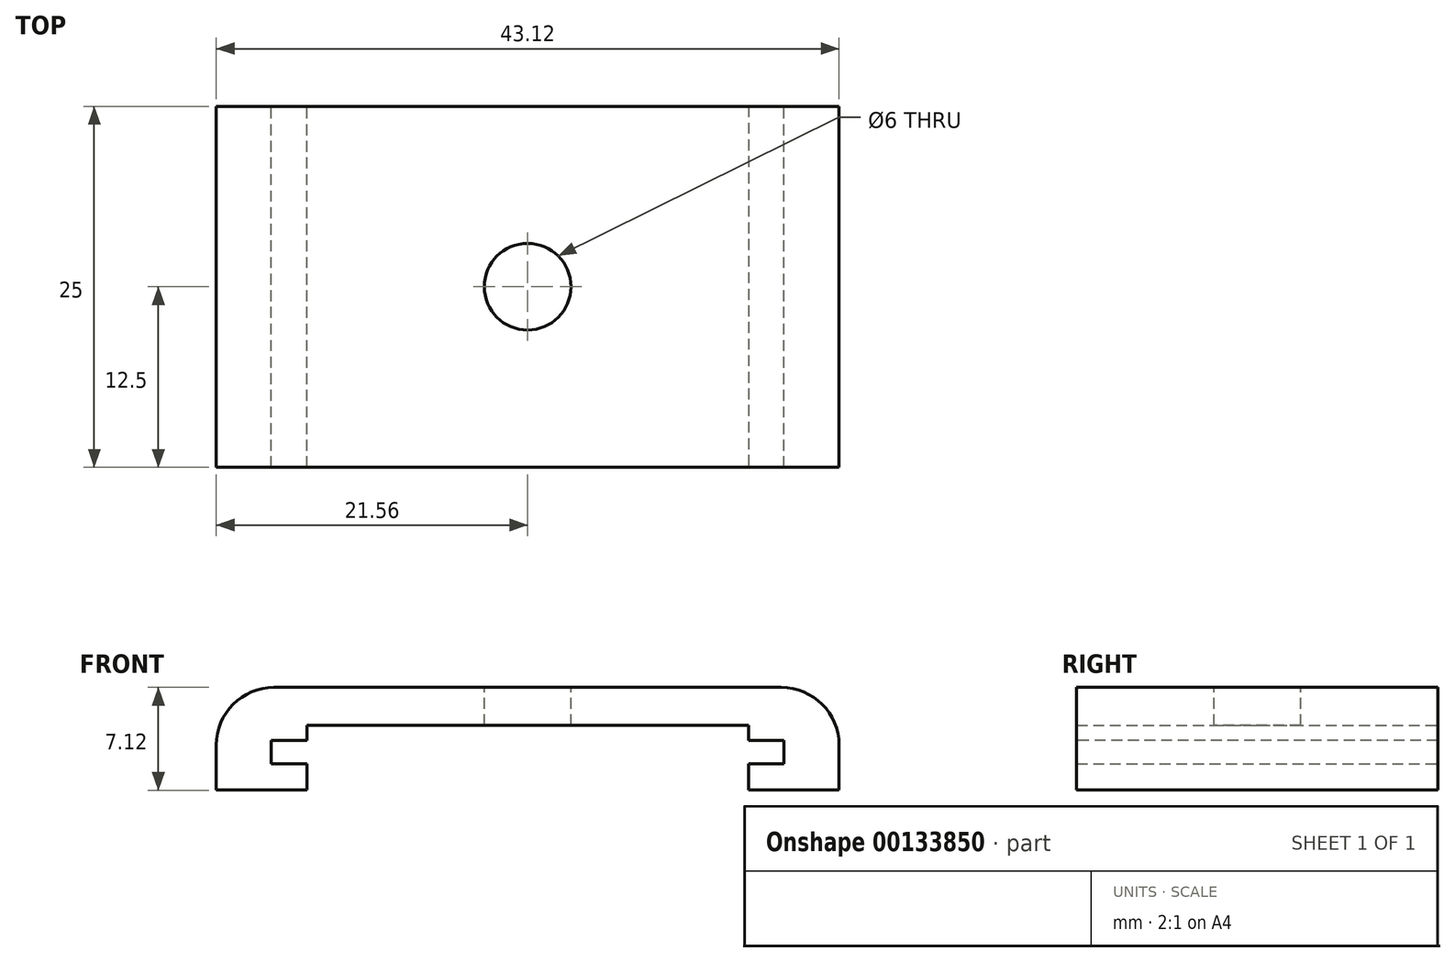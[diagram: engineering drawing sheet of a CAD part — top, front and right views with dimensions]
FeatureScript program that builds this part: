
annotation { "Feature Type Name" : "Feature", "Feature Type Description" : "" }
export const myFeature = defineFeature(function(context is Context, id is Id, definition is map)
    precondition{}
    {
        {
            var Q0;
            Q0=qCreatedBy(makeId("Front.planeOp"),FACE);
            var sketch = newSketch(context, id + "F0", { "sketchPlane" : qUnion([Q0])});
            skLineSegment(sketch, "E0", {"start": v(-17.75, 13.3) * mm, "end": v(-14.55, 13.3) * mm});
            skLineSegment(sketch, "E1", {"start": v(-13.65, 12.4) * mm, "end": v(-13.65, 0.9) * mm});
            skLineSegment(sketch, "E2", {"start": v(-12.75, 0) * mm, "end": v(0, 0) * mm});
            skLineSegment(sketch, "E3.0", {"start": v(-11.15, 1.6) * mm, "end": v(0, 1.6) * mm});
            skLineSegment(sketch, "E3.1", {"start": v(-12.05, 13.7) * mm, "end": v(-12.05, 2.5) * mm});
            skLineSegment(sketch, "E3.2", {"start": v(-17.75, 14.9) * mm, "end": v(-13.25, 14.9) * mm});
            skLineSegment(sketch, "E4", {"start": v(-17.75, 13.3) * mm, "end": v(-17.75, 14.9) * mm});
            skLineSegment(sketch, "E5.MirrorCS", {"start": v(11.15, 1.6) * mm, "end": v(0, 1.6) * mm});
            skLineSegment(sketch, "E6.MirrorCS", {"start": v(12.75, 0) * mm, "end": v(0, 0) * mm});
            skLineSegment(sketch, "E7.MirrorCS", {"start": v(12.05, 13.7) * mm, "end": v(12.05, 2.5) * mm});
            skLineSegment(sketch, "E8.MirrorCS", {"start": v(13.65, 12.4) * mm, "end": v(13.65, 0.9) * mm});
            skLineSegment(sketch, "E9.MirrorCS", {"start": v(17.75, 13.3) * mm, "end": v(14.55, 13.3) * mm});
            skLineSegment(sketch, "E10.MirrorCS", {"start": v(17.75, 14.9) * mm, "end": v(13.25, 14.9) * mm});
            skLineSegment(sketch, "E11.MirrorCS", {"start": v(17.75, 13.3) * mm, "end": v(17.75, 14.9) * mm});
            skPoint(sketch, "E12.visualSharp", {"position": v(-13.65, 13.3) * mm});
            skArc(sketch, "E12.filletArc", {"start": v(-13.65, 12.4) * mm, "mid": v(-13.91, 13.04) * mm, "end": v(-14.55, 13.3) * mm});
            skPoint(sketch, "E13.visualSharp", {"position": v(-12.05, 14.9) * mm});
            skArc(sketch, "E13.filletArc", {"start": v(-12.05, 13.7) * mm, "mid": v(-12.4, 14.55) * mm, "end": v(-13.25, 14.9) * mm});
            skPoint(sketch, "E14.visualSharp", {"position": v(-13.65, 0) * mm});
            skArc(sketch, "E14.filletArc", {"start": v(-13.65, 0.9) * mm, "mid": v(-13.39, 0.26) * mm, "end": v(-12.75, 0) * mm});
            skPoint(sketch, "E15.visualSharp", {"position": v(-12.05, 1.6) * mm});
            skArc(sketch, "E15.filletArc", {"start": v(-12.05, 2.5) * mm, "mid": v(-11.79, 1.86) * mm, "end": v(-11.15, 1.6) * mm});
            skPoint(sketch, "E16.visualSharp", {"position": v(13.65, 0) * mm});
            skArc(sketch, "E16.filletArc", {"start": v(12.75, 0) * mm, "mid": v(13.39, 0.26) * mm, "end": v(13.65, 0.9) * mm});
            skPoint(sketch, "E17.visualSharp", {"position": v(12.05, 1.6) * mm});
            skArc(sketch, "E17.filletArc", {"start": v(11.15, 1.6) * mm, "mid": v(11.79, 1.86) * mm, "end": v(12.05, 2.5) * mm});
            skPoint(sketch, "E18.visualSharp", {"position": v(12.05, 14.9) * mm});
            skArc(sketch, "E18.filletArc", {"start": v(13.25, 14.9) * mm, "mid": v(12.4, 14.55) * mm, "end": v(12.05, 13.7) * mm});
            skPoint(sketch, "E19.visualSharp", {"position": v(13.65, 13.3) * mm});
            skArc(sketch, "E19.filletArc", {"start": v(14.55, 13.3) * mm, "mid": v(13.91, 13.04) * mm, "end": v(13.65, 12.4) * mm});
            skSolve(sketch);
        }
        {
            var Q0;
            Q0 = qSketchRegion(id + "F0", true);
            extrude(context, id + "F1", {"entities" : qUnion([Q0]), "depth" : 50 * mm});
        }
        {
            var Q0;
            Q0=qCreatedBy(makeId("Front.planeOp"),FACE);
            var sketch = newSketch(context, id + "F2", { "sketchPlane" : qUnion([Q0])});
            skLineSegment(sketch, "E20", {"start": v(-15.28, 11.46) * mm, "end": v(-21.56, 11.46) * mm});
            skLineSegment(sketch, "E21", {"start": v(-21.56, 11.46) * mm, "end": v(-21.56, 14.58) * mm});
            skLineSegment(sketch, "E22", {"start": v(-17.56, 18.58) * mm, "end": v(0, 18.58) * mm});
            skLineSegment(sketch, "E23", {"start": v(-15.28, 11.46) * mm, "end": v(-15.28, 15.95) * mm});
            skLineSegment(sketch, "E24", {"start": v(-15.28, 15.95) * mm, "end": v(0, 15.95) * mm});
            skPoint(sketch, "E25.visualSharp", {"position": v(-21.56, 18.58) * mm});
            skArc(sketch, "E25.filletArc", {"start": v(-17.56, 18.58) * mm, "mid": v(-20.4, 17.4) * mm, "end": v(-21.56, 14.58) * mm});
            skLineSegment(sketch, "E26.MirrorCS", {"start": v(17.56, 18.58) * mm, "end": v(0, 18.58) * mm});
            skArc(sketch, "E27.MirrorCS", {"start": v(17.56, 18.58) * mm, "mid": v(20.4, 17.4) * mm, "end": v(21.56, 14.58) * mm});
            skLineSegment(sketch, "E28.MirrorCS", {"start": v(21.56, 11.46) * mm, "end": v(21.56, 14.58) * mm});
            skLineSegment(sketch, "E29.MirrorCS", {"start": v(15.28, 11.46) * mm, "end": v(21.56, 11.46) * mm});
            skLineSegment(sketch, "E30.MirrorCS", {"start": v(15.28, 15.95) * mm, "end": v(0, 15.95) * mm});
            skLineSegment(sketch, "E31.MirrorCS", {"start": v(15.28, 11.46) * mm, "end": v(15.28, 15.95) * mm});
            skSolve(sketch);
        }
        {
            var Q0;
            Q0 = qSketchRegion(id + "F2", true);
            extrude(context, id + "F3", {"entities" : qUnion([Q0]), "depth" : 25 * mm});
        }
        {
            var Q0;
            Q0=makeQuery(id+"F1.opExtrude","SWEPT_BODY",BODY,{"disambiguationData":[OSD([sQuery(id+"F0.wireOp",EDGE,"E0"),sQuery(id+"F0.wireOp",EDGE,"E1"),sQuery(id+"F0.wireOp",EDGE,"E2"),sQuery(id+"F0.wireOp",EDGE,"E3.0"),sQuery(id+"F0.wireOp",EDGE,"E3.1"),sQuery(id+"F0.wireOp",EDGE,"E3.2"),sQuery(id+"F0.wireOp",EDGE,"E4"),sQuery(id+"F0.wireOp",EDGE,"E5.MirrorCS"),sQuery(id+"F0.wireOp",EDGE,"E6.MirrorCS"),sQuery(id+"F0.wireOp",EDGE,"E7.MirrorCS"),sQuery(id+"F0.wireOp",EDGE,"E8.MirrorCS"),sQuery(id+"F0.wireOp",EDGE,"E9.MirrorCS"),sQuery(id+"F0.wireOp",EDGE,"E10.MirrorCS"),sQuery(id+"F0.wireOp",EDGE,"E11.MirrorCS"),sQuery(id+"F0.wireOp",EDGE,"E12.filletArc"),sQuery(id+"F0.wireOp",EDGE,"E13.filletArc"),sQuery(id+"F0.wireOp",EDGE,"E14.filletArc"),sQuery(id+"F0.wireOp",EDGE,"E15.filletArc"),sQuery(id+"F0.wireOp",EDGE,"E16.filletArc"),sQuery(id+"F0.wireOp",EDGE,"E17.filletArc"),sQuery(id+"F0.wireOp",EDGE,"E18.filletArc"),sQuery(id+"F0.wireOp",EDGE,"E19.filletArc")])]});
            var Q1;
            Q1=makeQuery(id+"F3.opExtrude","SWEPT_BODY",BODY,{"disambiguationData":[OSD([sQuery(id+"F2.wireOp",EDGE,"E20"),sQuery(id+"F2.wireOp",EDGE,"E21"),sQuery(id+"F2.wireOp",EDGE,"E22"),sQuery(id+"F2.wireOp",EDGE,"E23"),sQuery(id+"F2.wireOp",EDGE,"E24"),sQuery(id+"F2.wireOp",EDGE,"E25.filletArc"),sQuery(id+"F2.wireOp",EDGE,"E26.MirrorCS"),sQuery(id+"F2.wireOp",EDGE,"E27.MirrorCS"),sQuery(id+"F2.wireOp",EDGE,"E28.MirrorCS"),sQuery(id+"F2.wireOp",EDGE,"E29.MirrorCS"),sQuery(id+"F2.wireOp",EDGE,"E30.MirrorCS"),sQuery(id+"F2.wireOp",EDGE,"E31.MirrorCS")])]});
            booleanBodies(context, id + "F4", {"operationType" : BooleanOperationType.SUBTRACTION, "tools" : qUnion([Q0]), "targets" : qUnion([Q1])});
        }
        {
            var Q0;
            Q0=makeQuery(id+"F3.opExtrude","SWEPT_FACE",FACE,{"disambiguationData":[OSD([sQuery(id+"F2.wireOp",EDGE,"E22"),sQuery(id+"F2.wireOp",EDGE,"E26.MirrorCS")])]});
            var sketch = newSketch(context, id + "F5", { "sketchPlane" : qUnion([Q0])});
            skPoint(sketch, "E32", {"position": v(0, -12.5) * mm});
            skLineSegment(sketch, "E33", {"start": v(0, 0) * mm, "end": v(0, -25) * mm, "construction": true});
            skSolve(sketch);
        }
        {
            var Q0;
            Q0=sQuery(id+"F5.wireOp",VERTEX,"E32");
            var Q1;
            Q1=makeQuery(id+"F3.opExtrude","SWEPT_BODY",BODY,{"disambiguationData":[OSD([sQuery(id+"F2.wireOp",EDGE,"E20"),sQuery(id+"F2.wireOp",EDGE,"E21"),sQuery(id+"F2.wireOp",EDGE,"E22"),sQuery(id+"F2.wireOp",EDGE,"E23"),sQuery(id+"F2.wireOp",EDGE,"E24"),sQuery(id+"F2.wireOp",EDGE,"E25.filletArc"),sQuery(id+"F2.wireOp",EDGE,"E26.MirrorCS"),sQuery(id+"F2.wireOp",EDGE,"E27.MirrorCS"),sQuery(id+"F2.wireOp",EDGE,"E28.MirrorCS"),sQuery(id+"F2.wireOp",EDGE,"E29.MirrorCS"),sQuery(id+"F2.wireOp",EDGE,"E30.MirrorCS"),sQuery(id+"F2.wireOp",EDGE,"E31.MirrorCS")])]});
            hole(context, id + "F6", {"style" : HoleStyle.SIMPLE, "endStyle" : HoleEndStyle.THROUGH, "holeDiameter" : 6 * mm, "locations" : qUnion([Q0]), "scope" : qUnion([Q1]), "isTappedThrough" : true});
        }
    });
